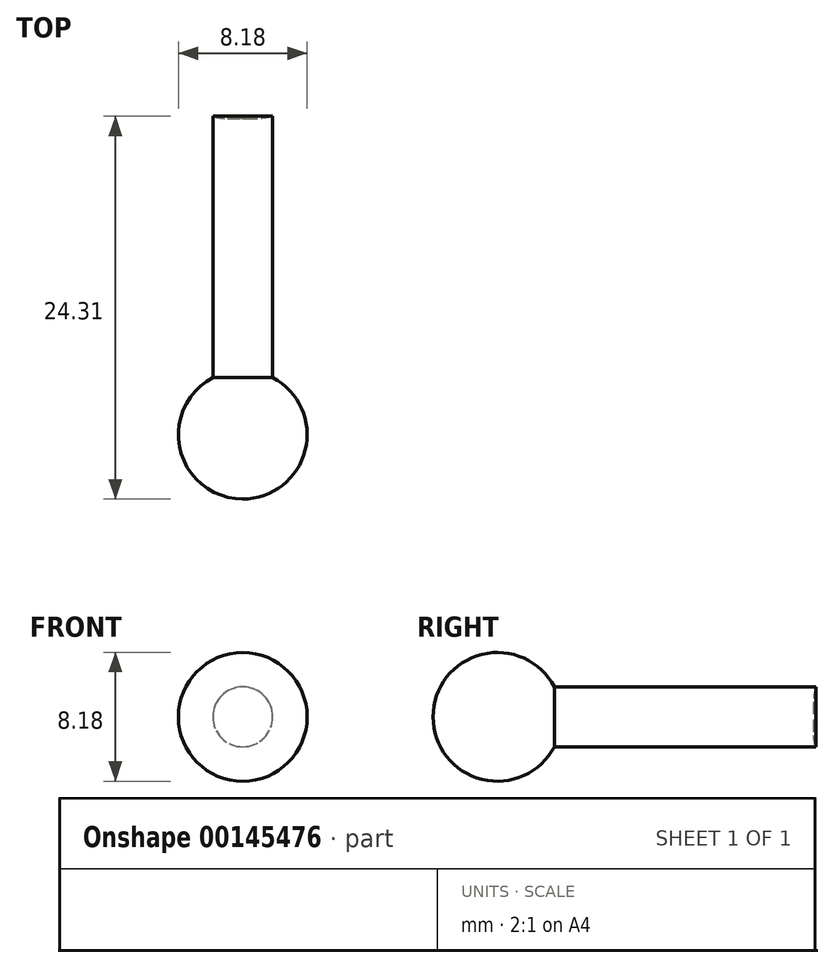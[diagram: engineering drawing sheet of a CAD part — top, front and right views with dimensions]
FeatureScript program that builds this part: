
annotation { "Feature Type Name" : "Feature", "Feature Type Description" : "" }
export const myFeature = defineFeature(function(context is Context, id is Id, definition is map)
    precondition{}
    {
        {
            var Q0;
            Q0=qCreatedBy(makeId("Top.planeOp"),FACE);
            var sketch = newSketch(context, id + "F0", { "sketchPlane" : qUnion([Q0])});
            skLineSegment(sketch, "E0", {"start": v(-36.48, -16.6) * mm, "end": v(-36.48, 0) * mm});
            skArc(sketch, "E1", {"start": v(-36.48, -16.6) * mm, "mid": v(-38.55, -21.2) * mm, "end": v(-34.58, -24.31) * mm});
            skArc(sketch, "E2", {"start": v(-34.58, 6.1) * mm, "mid": v(-38.58, 4) * mm, "end": v(-36.48, 0) * mm});
            skLineSegment(sketch, "E3", {"start": v(-34.58, -24.31) * mm, "end": v(-34.58, 6.1) * mm});
            skSolve(sketch);
        }
        {
            var Q0;
            Q0=makeQuery(id+"F0.imprint","IMPRINT",FACE,{"disambiguationData":[TD([[makeQuery(id+"F0.imprint","IMPRINT",EDGE,{"derivedFrom":sQuery(id+"F0.wireOp",EDGE,"E0")}),-1.0]])]});
            var Q1;
            Q1=sQuery(id+"F0.wireOp",EDGE,"E3");
            revolve(context, id + "F1", {"entities" : qUnion([Q0]), "axis" : qUnion([Q1]), "revolveType" : RevolveType.FULL});
        }
    });
